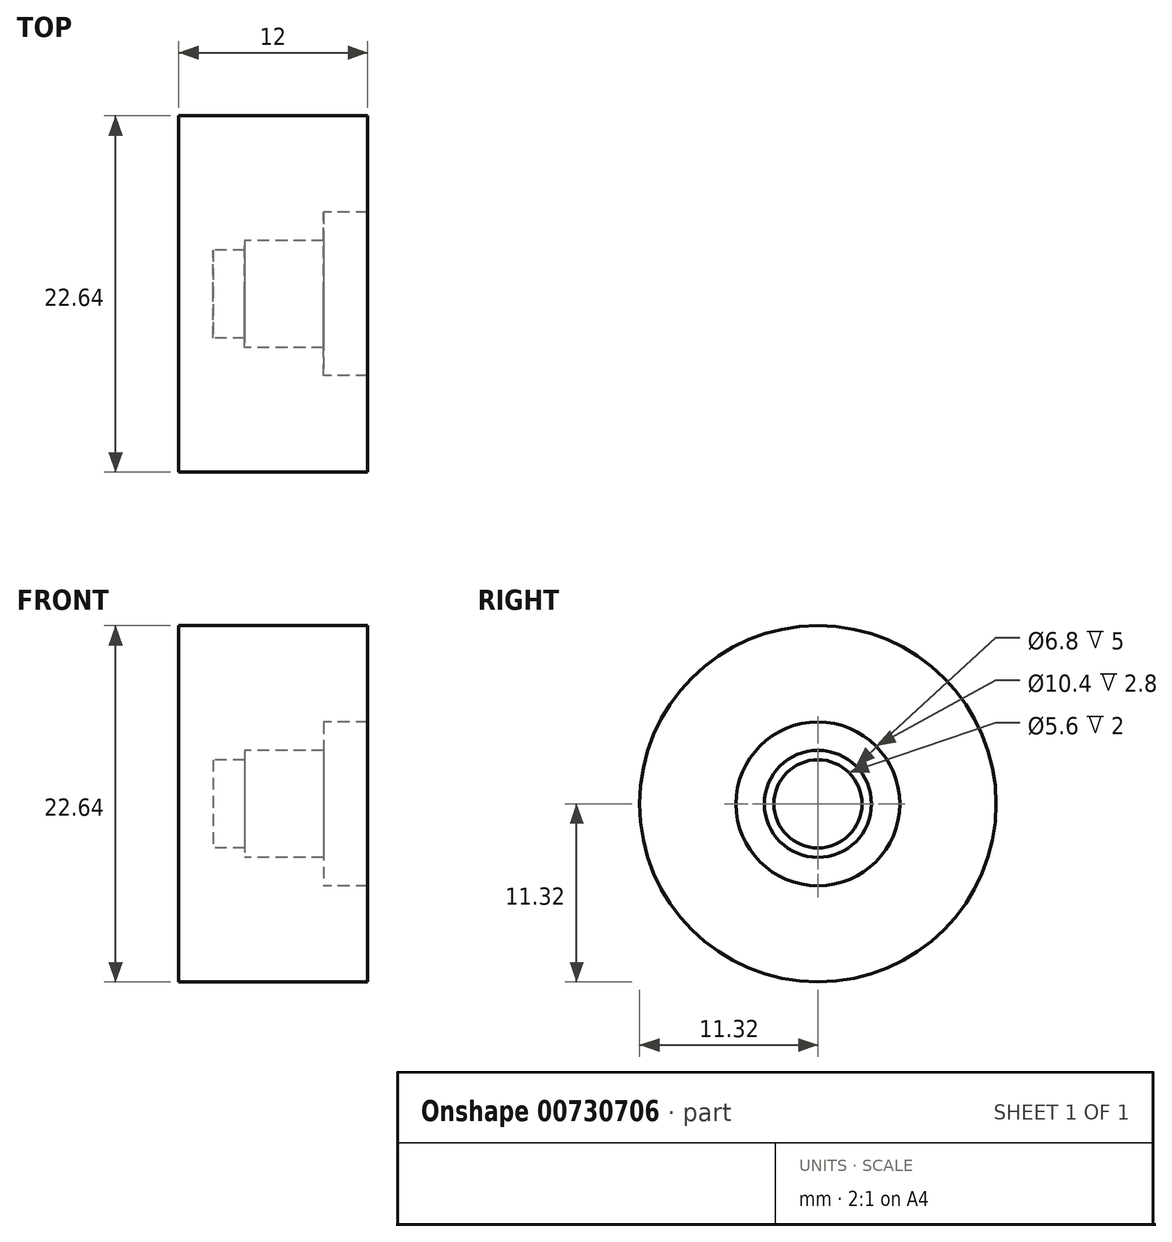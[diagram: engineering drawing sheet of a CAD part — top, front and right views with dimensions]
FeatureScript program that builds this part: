
annotation { "Feature Type Name" : "Feature", "Feature Type Description" : "" }
export const myFeature = defineFeature(function(context is Context, id is Id, definition is map)
    precondition{}
    {
        {
            var Q0;
            Q0=qCreatedBy(makeId("Front.planeOp"),FACE);
            var sketch = newSketch(context, id + "F0", { "sketchPlane" : qUnion([Q0])});
            skLineSegment(sketch, "E0", {"start": v(-7.8, 2.8) * mm, "end": v(-7.8, 3.4) * mm});
            skLineSegment(sketch, "E1", {"start": v(-7.8, 3.4) * mm, "end": v(-2.8, 3.4) * mm});
            skLineSegment(sketch, "E2", {"start": v(-2.8, 3.4) * mm, "end": v(-2.8, 5.2) * mm});
            skLineSegment(sketch, "E3", {"start": v(-2.8, 5.2) * mm, "end": v(0, 5.2) * mm});
            skLineSegment(sketch, "E4", {"start": v(-26.14, 0) * mm, "end": v(33.96, 0) * mm});
            skLineSegment(sketch, "E5", {"start": v(-12, 11.32) * mm, "end": v(0, 11.32) * mm});
            skLineSegment(sketch, "E6", {"start": v(0, 11.32) * mm, "end": v(0, 5.2) * mm});
            skLineSegment(sketch, "E7", {"start": v(-12, 11.32) * mm, "end": v(-12, 0) * mm});
            skLineSegment(sketch, "E8", {"start": v(-12, 0) * mm, "end": v(-9.8, 0) * mm});
            skLineSegment(sketch, "E9", {"start": v(-9.8, 0) * mm, "end": v(-9.8, 2.8) * mm});
            skLineSegment(sketch, "E10", {"start": v(-9.8, 2.8) * mm, "end": v(-7.8, 2.8) * mm});
            skSolve(sketch);
        }
        {
            var Q0;
            Q0=makeQuery(id+"F0.imprint","IMPRINT",FACE,{"disambiguationData":[TD([[makeQuery(id+"F0.imprint","IMPRINT",EDGE,{"derivedFrom":sQuery(id+"F0.wireOp",EDGE,"E0")}),1.0]])]});
            var Q1;
            Q1=sQuery(id+"F0.wireOp",EDGE,"E4");
            revolve(context, id + "F1", {"surfaceOperationType" : NewSurfaceOperationType.NEW, "entities" : qUnion([Q0]), "axis" : qUnion([Q1]), "revolveType" : RevolveType.FULL});
        }
    });
